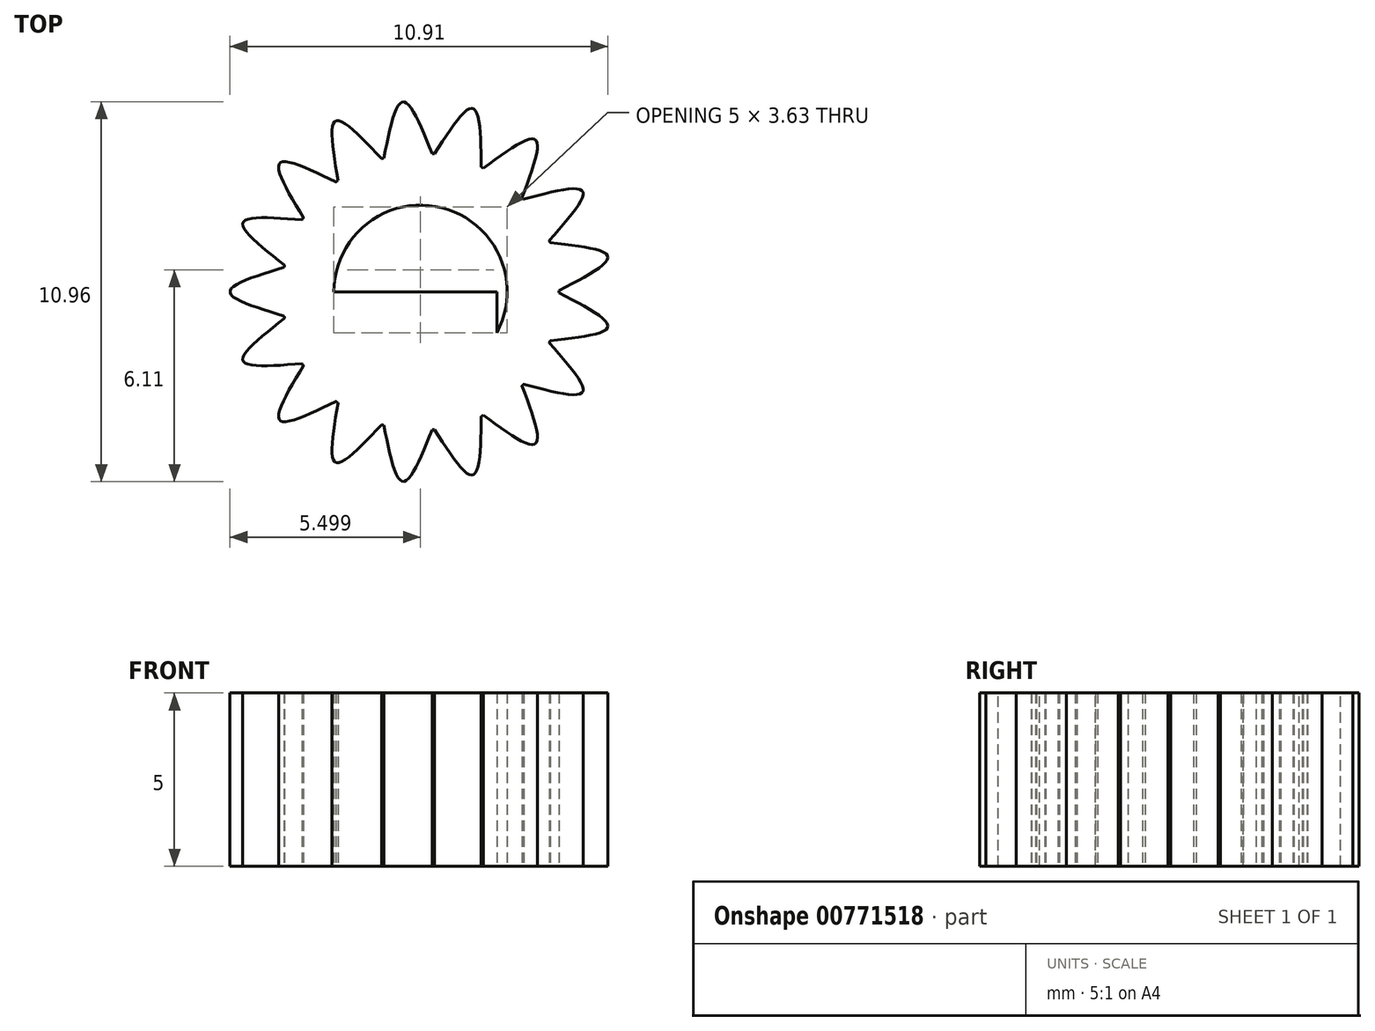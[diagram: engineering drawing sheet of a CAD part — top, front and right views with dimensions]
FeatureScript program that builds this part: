
annotation { "Feature Type Name" : "Feature", "Feature Type Description" : "" }
export const myFeature = defineFeature(function(context is Context, id is Id, definition is map)
    precondition{}
    {
        {
            var Q0;
            Q0=qCreatedBy(makeId("Top.planeOp"),FACE);
            var sketch = newSketch(context, id + "F0", { "sketchPlane" : qUnion([Q0])});
            skLineSegment(sketch, "E0", {"start": v(0, 0) * mm, "end": v(5.5, 0) * mm, "construction": true});
            skLineSegment(sketch, "E1", {"start": v(5.5, 0) * mm, "end": v(-5.5, 0) * mm, "construction": true});
            skCircle(sketch, "E2", {"center": v(0, 0) * mm, "radius": 2.5 * mm});
            skCircle(sketch, "E3", {"center": v(0, 0) * mm, "radius": 4 * mm});
            skLineSegment(sketch, "E4", {"start": v(-4, 0) * mm, "end": v(-4, 0.7) * mm, "construction": true});
            skLineSegment(sketch, "E5", {"start": v(-4, 0.7) * mm, "end": v(-4, -0.7) * mm, "construction": true});
            skLineSegment(sketch, "E6", {"start": v(-4, -0.7) * mm, "end": v(-3.94, -0.7) * mm, "construction": true});
            skLineSegment(sketch, "E7", {"start": v(-3.94, -0.7) * mm, "end": v(-3.94, 0.7) * mm, "construction": true});
            skLineSegment(sketch, "E8", {"start": v(-3.94, 0.7) * mm, "end": v(-4, 0.7) * mm, "construction": true});
            skFitSpline(sketch, "E9", {"points": [v(-3.94, -0.7) * mm, v(-5.5, 0) * mm, v(-3.94, 0.7) * mm], "startDerivative": vector(-4.69, 1.4) * mm, "endDerivative": vector(4.69, 1.4) * mm});
            skLineSegment(sketch, "E10", {"start": v(-2.5, 0) * mm, "end": v(2.2, 0) * mm});
            skLineSegment(sketch, "E11", {"start": v(2.2, 0) * mm, "end": v(2.2, 1.19) * mm});
            skLineSegment(sketch, "E12", {"start": v(2.2, 1.19) * mm, "end": v(2.2, -1.19) * mm});
            skSolve(sketch);
        }
        {
            var Q0;
            Q0=makeQuery(id+"F0.imprint","IMPRINT",FACE,{"disambiguationData":[TD([[makeQuery(id+"F0.imprint","IMPRINT",EDGE,{"derivedFrom":sQuery(id+"F0.wireOp",EDGE,"E2")}),-1.0]])]});
            var Q1;
            {var subQ0=sQuery(id+"F0.wireOp",EDGE,"E9");Q1=makeQuery(id+"F0.imprint","IMPRINT",FACE,{"disambiguationData":[TD([[makeQuery(id+"F0.imprint","IMPRINT",EDGE,{"derivedFrom":subQ0}),-1.0]])]});}
            extrude(context, id + "F1", {"entities" : qUnion([Q0, Q1]), "depth" : 5 * mm, "offsetDistance" : 25 * mm});
        }
        {
            var Q0;
            Q0=makeQuery(id+"F1.opExtrude","SWEPT_BODY",BODY,{"disambiguationData":[OSD([sQuery(id+"F0.wireOp",EDGE,"E2"),sQuery(id+"F0.wireOp",EDGE,"E3"),sQuery(id+"F0.wireOp",EDGE,"E9")])]});
            var Q1;
            Q1=makeQuery(id+"F1.opExtrude","CAP_EDGE",EDGE,{"disambiguationData":[OSD([sQuery(id+"F0.wireOp",EDGE,"E2")])],"isStart":false});
            circularPattern(context, id + "F2", {"entities" : qUnion([Q0]), "axis" : qUnion([Q1]), "angle" : 360 * degree, "instanceCount" : 17, "equalSpace" : true});
        }
        {
            var Q0;
            {var subQ0=sQuery(id+"F0.wireOp",EDGE,"E12");var subQ1=sQuery(id+"F0.wireOp",EDGE,"E2");var subQ2=makeQuery(id+"F0.imprint","INTERSECT",VERTEX,{"disambiguationData":[OD(0.0)],"derivedFrom":[subQ1,subQ0]});Q0=makeQuery(id+"F0.imprint","IMPRINT",FACE,{"disambiguationData":[TD([[makeQuery(id+"F0.imprint","IMPRINT",EDGE,{"disambiguationData":[TD([[subQ2,1.0]])],"derivedFrom":subQ1}),1.0]])]});}
            extrude(context, id + "F3", {"entities" : qUnion([Q0]), "operationType" : NewBodyOperationType.ADD, "depth" : 5 * mm, "offsetDistance" : 25 * mm});
        }
    });
